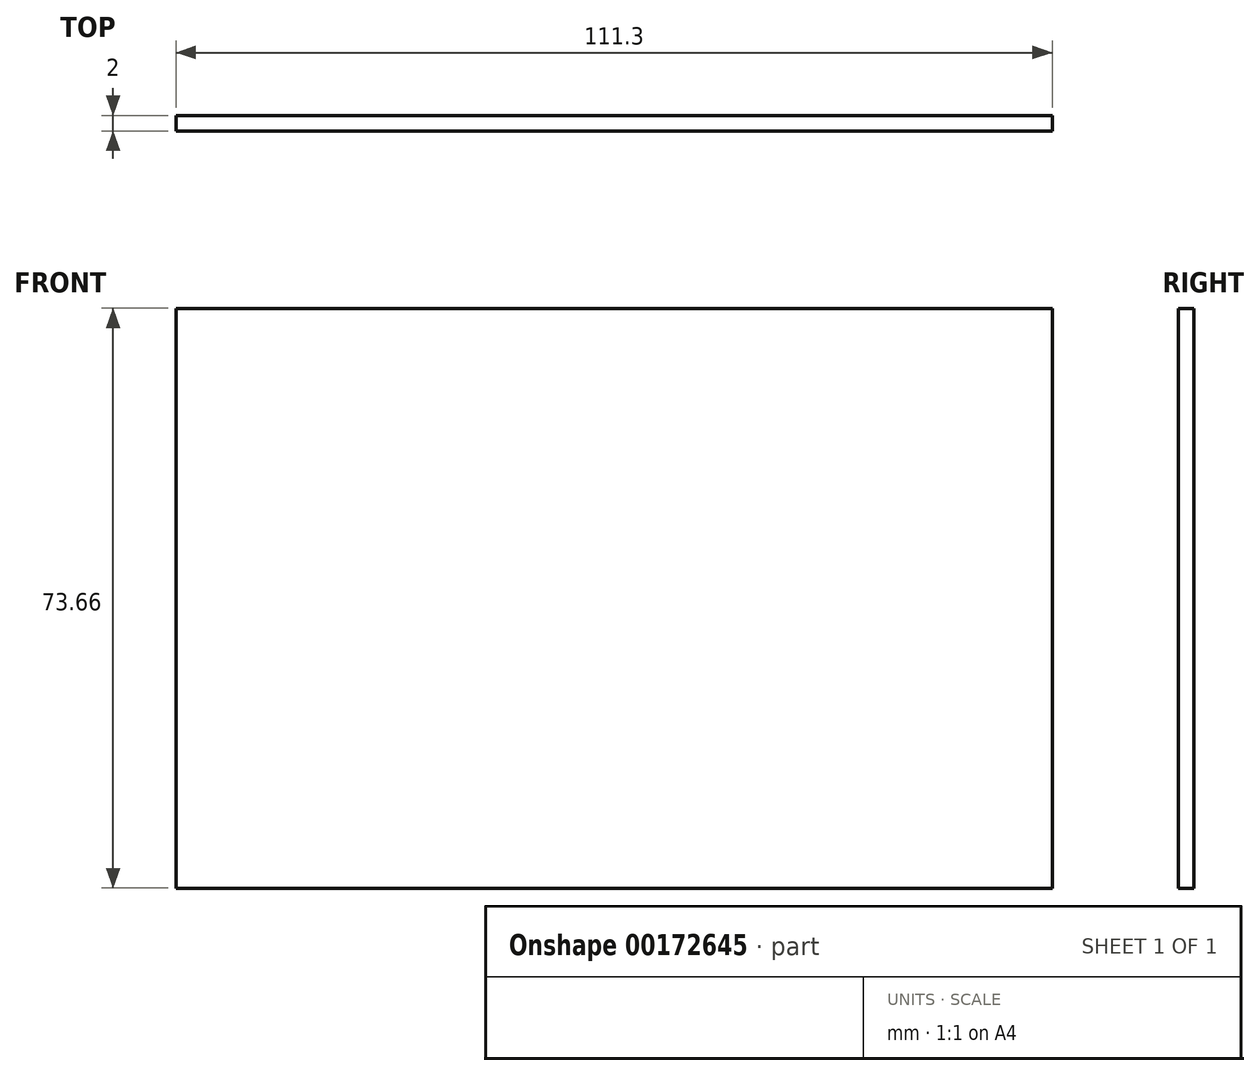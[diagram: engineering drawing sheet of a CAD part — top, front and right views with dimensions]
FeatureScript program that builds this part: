
annotation { "Feature Type Name" : "Feature", "Feature Type Description" : "" }
export const myFeature = defineFeature(function(context is Context, id is Id, definition is map)
    precondition{}
    {
        {
            var Q0;
            Q0=qCreatedBy(makeId("Front.planeOp"),FACE);
            var sketch = newSketch(context, id + "F0", { "sketchPlane" : qUnion([Q0])});
            skLineSegment(sketch, "E0.bottom", {"start": v(-57.5, 38.22) * mm, "end": v(53.8, 38.22) * mm});
            skLineSegment(sketch, "E0.top", {"start": v(-57.5, -35.44) * mm, "end": v(53.8, -35.44) * mm});
            skLineSegment(sketch, "E0.left", {"start": v(-57.5, 38.22) * mm, "end": v(-57.5, -35.44) * mm});
            skLineSegment(sketch, "E0.right", {"start": v(53.8, 38.22) * mm, "end": v(53.8, -35.44) * mm});
            skSolve(sketch);
        }
        {
            var Q0;
            Q0=makeQuery(id+"F0.imprint","IMPRINT",FACE,{"disambiguationData":[TD([[makeQuery(id+"F0.imprint","IMPRINT",EDGE,{"derivedFrom":sQuery(id+"F0.wireOp",EDGE,"E0.bottom")}),-1.0]])]});
            extrude(context, id + "F1", {"entities" : qUnion([Q0]), "depth" : 2 * mm});
        }
    });
